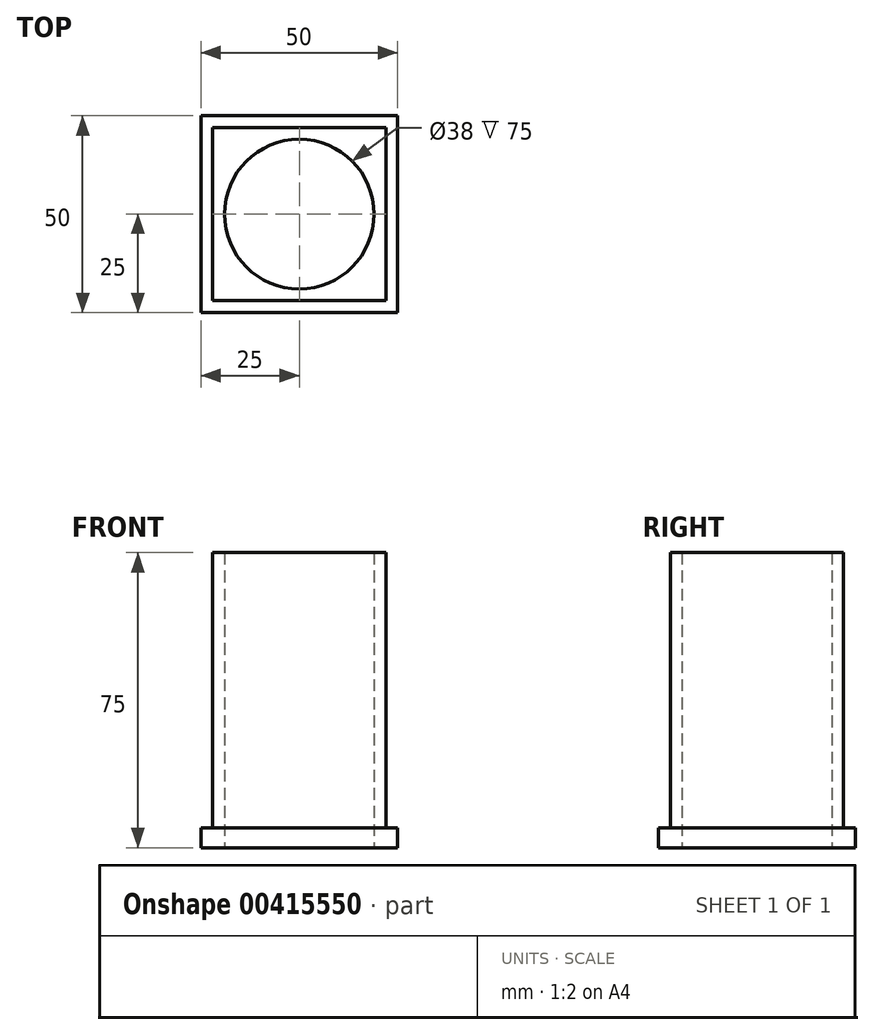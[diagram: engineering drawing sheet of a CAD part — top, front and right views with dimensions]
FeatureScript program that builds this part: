
annotation { "Feature Type Name" : "Feature", "Feature Type Description" : "" }
export const myFeature = defineFeature(function(context is Context, id is Id, definition is map)
    precondition{}
    {
        {
            var Q0;
            Q0=qCreatedBy(makeId("Top.planeOp"),FACE);
            var sketch = newSketch(context, id + "F0", { "sketchPlane" : qUnion([Q0])});
            skLineSegment(sketch, "E0.bottom", {"start": v(25, 25) * mm, "end": v(-25, 25) * mm});
            skLineSegment(sketch, "E0.top", {"start": v(25, -25) * mm, "end": v(-25, -25) * mm});
            skLineSegment(sketch, "E0.left", {"start": v(25, 25) * mm, "end": v(25, -25) * mm});
            skLineSegment(sketch, "E0.right", {"start": v(-25, 25) * mm, "end": v(-25, -25) * mm});
            skPoint(sketch, "E0.middle", {"position": v(0, 0) * mm});
            skSolve(sketch);
        }
        {
            var Q0;
            Q0 = qSketchRegion(id + "F0", true);
            extrude(context, id + "F1", {"entities" : qUnion([Q0]), "depth" : 5 * mm});
        }
        {
            var Q0;
            Q0=makeQuery(id+"F1.opExtrude","CAP_FACE",FACE,{"disambiguationData":[OSD([sQuery(id+"F0.wireOp",EDGE,"E0.bottom"),sQuery(id+"F0.wireOp",EDGE,"E0.top"),sQuery(id+"F0.wireOp",EDGE,"E0.left"),sQuery(id+"F0.wireOp",EDGE,"E0.right")])],"isStart":false});
            var sketch = newSketch(context, id + "F2", { "sketchPlane" : qUnion([Q0])});
            skLineSegment(sketch, "E1.bottom", {"start": v(22, 22) * mm, "end": v(-22, 22) * mm});
            skLineSegment(sketch, "E1.top", {"start": v(22, -22) * mm, "end": v(-22, -22) * mm});
            skLineSegment(sketch, "E1.left", {"start": v(22, 22) * mm, "end": v(22, -22) * mm});
            skLineSegment(sketch, "E1.right", {"start": v(-22, 22) * mm, "end": v(-22, -22) * mm});
            skPoint(sketch, "E1.middle", {"position": v(0, 0) * mm});
            skCircle(sketch, "E2", {"center": v(0, 0) * mm, "radius": 19 * mm});
            skSolve(sketch);
        }
        {
            var Q0;
            Q0 = qSketchRegion(id + "F2", true);
            extrude(context, id + "F3", {"entities" : qUnion([Q0]), "operationType" : NewBodyOperationType.ADD, "depth" : 70 * mm});
        }
        {
            var Q0;
            Q0=makeQuery(id+"F3.boolean.opBoolean","SPLIT",FACE,{"disambiguationData":[TD([makeQuery(id+"F3.opExtrude","SWEPT_FACE",FACE,{"disambiguationData":[OSD([sQuery(id+"F2.wireOp",EDGE,"E2")])]})])],"derivedFrom":makeQuery(id+"F1.opExtrude","CAP_FACE",FACE,{"disambiguationData":[OSD([sQuery(id+"F0.wireOp",EDGE,"E0.bottom"),sQuery(id+"F0.wireOp",EDGE,"E0.top"),sQuery(id+"F0.wireOp",EDGE,"E0.left"),sQuery(id+"F0.wireOp",EDGE,"E0.right")])],"isStart":false})});
            extrude(context, id + "F4", {"entities" : qUnion([Q0]), "operationType" : NewBodyOperationType.REMOVE, "oppositeDirection" : true, "depth" : 78.5 * mm});
        }
    });
